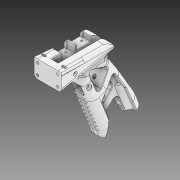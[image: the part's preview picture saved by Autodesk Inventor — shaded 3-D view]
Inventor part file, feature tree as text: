
AUTODESK INVENTOR PART (.ipt)
format: ipt  version: 2020 (Build 240168000, 168)  size: 1,707,520 bytes
history: native  units: in
note: dims shown in document units (in); Inventor stores cm internally (conversion verified against a paired STEP export)
features: extrude x10, sketch x10, fillet x1, plane x1, imported_body x1
ambient origin geometry x8: Origin, YZ Plane, XZ Plane, XY Plane, X Axis, Y Axis, Z Axis, Center Point
bodies: Solid1 (feature_tree)
feature tree (23):
  extrude  "Extrusion1"  Depth=0.1575in
  extrude  "Extrusion4"  Depth=0.3937in TaperAngle=0.0deg
  fillet  "Fillet1"  Radius=0.1378in
  extrude  "Extrusion5"  Depth=0.5906in
  extrude  "Extrusion6"  Depth=0.4724in TaperAngle=0.0deg
  plane  "Work Plane1"
  extrude  "Extrusion7"  Depth=0.2244in
  extrude  "Extrusion8"  Depth=0.4331in
  extrude  "Extrusion9"  Depth=0.9449in
  extrude  "Extrusion10"  Depth=0.3937in
  extrude  "Extrusion11"  Depth=0.0787in TaperAngle=0.0deg
  extrude  "Test Cut"  Depth=0.0394in
  sketch  "Sketch1"  dims[d0=0.0in d1=0.0in d2=0.1575in]
  sketch  "Sketch5"  dims[d7=3.3563in d8=0.0in d9=0.3937in d10=0.0in d11=0.1378in]
  sketch  "Sketch6"  dims[d12=1.1024in d13=0.5906in]
  sketch  "Sketch7"  dims[d14=0.4724in d15=0.5906in d16=0.0in]
  sketch  "Sketch8"  dims[d17=-0.3937in d18=0.2244in]
  sketch  "Sketch10"  dims[d19=0.1024in d20=0.0in d21=0.4331in]
  sketch  "Sketch11"  dims[d22=0.7874in d23=0.9449in]
  sketch  "Sketch12"  dims[d24=0.3937in d25=0.0in d26=0.7874in]
  sketch  "Sketch13"  dims[d27=0.0787in d28=0.2756in d29=0.0in]
  sketch  "Sketch14"  dims[d30=0.0394in d31=0.0394in d32=0.0394in d33=0.0394in d34=0.3642in d35=0.1181in d36=0.0984in d37=0.1969in d38=0.0in d39=0.3642in d40=0.1181in d41=0.0984in d42=0.1772in d43=0.0in d44=0.0in d45=0.0in]
  imported_body  "Base1"
